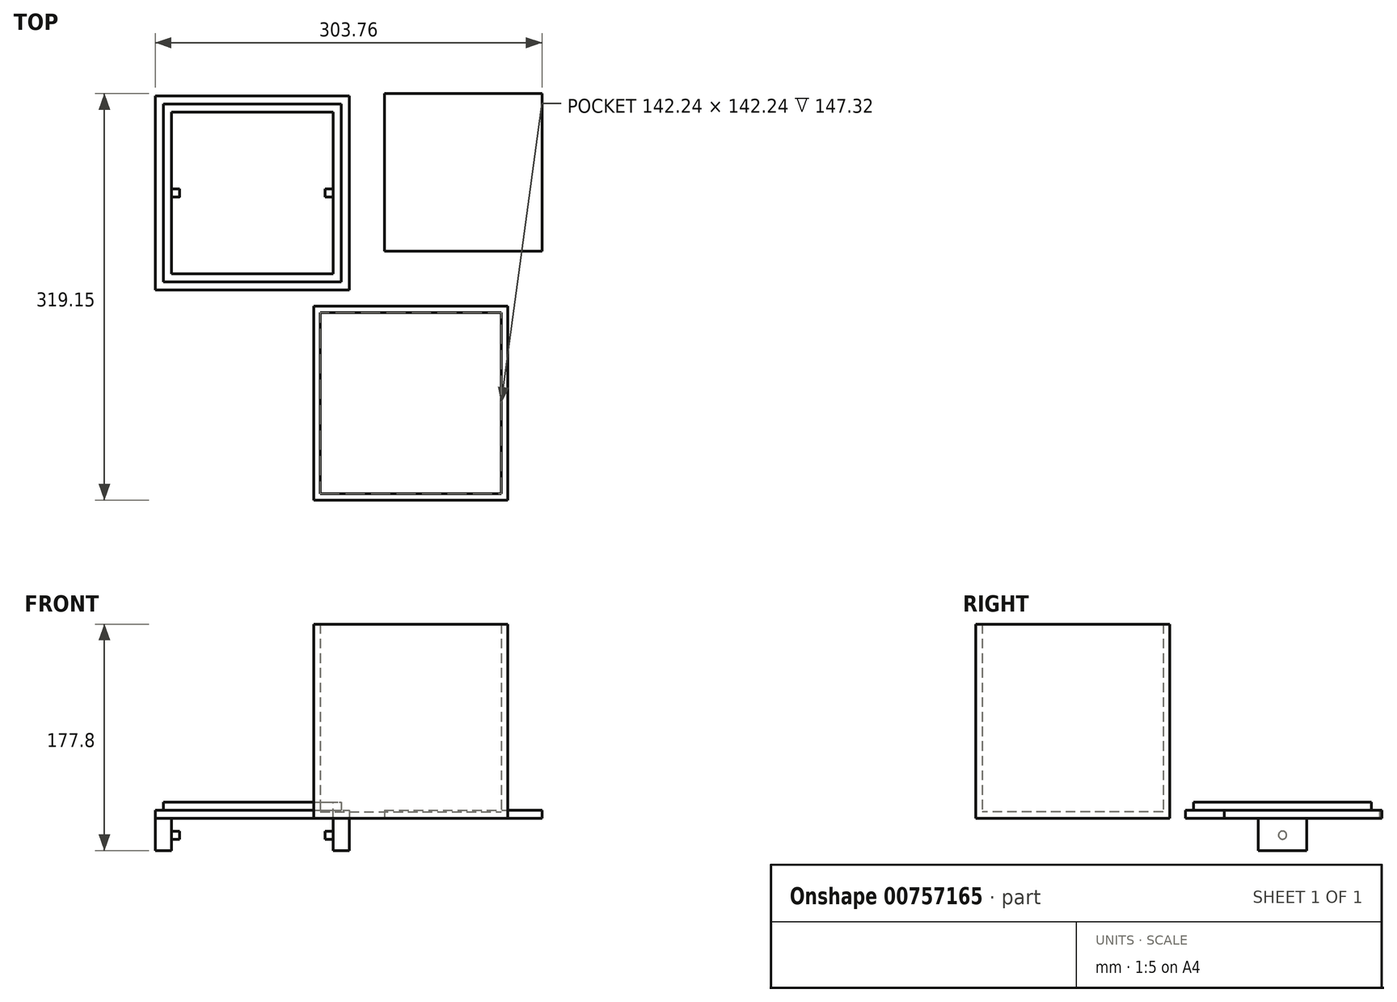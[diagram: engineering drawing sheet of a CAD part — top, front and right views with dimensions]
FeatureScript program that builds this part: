
annotation { "Feature Type Name" : "Feature", "Feature Type Description" : "" }
export const myFeature = defineFeature(function(context is Context, id is Id, definition is map)
    precondition{}
    {
        {
            var Q0;
            Q0=qCreatedBy(makeId("Top.planeOp"),FACE);
            var sketch = newSketch(context, id + "F0", { "sketchPlane" : qUnion([Q0])});
            skLineSegment(sketch, "E0.bottom", {"start": v(-92.32, 84.12) * mm, "end": v(60.08, 84.12) * mm});
            skLineSegment(sketch, "E0.top", {"start": v(-92.32, -68.28) * mm, "end": v(60.08, -68.28) * mm});
            skLineSegment(sketch, "E0.left", {"start": v(-92.32, 84.12) * mm, "end": v(-92.32, -68.28) * mm});
            skLineSegment(sketch, "E0.right", {"start": v(60.08, 84.12) * mm, "end": v(60.08, -68.28) * mm});
            skSolve(sketch);
        }
        {
            var Q0;
            Q0=makeQuery(id+"F0.imprint","IMPRINT",FACE,{"disambiguationData":[TD([[makeQuery(id+"F0.imprint","IMPRINT",EDGE,{"derivedFrom":sQuery(id+"F0.wireOp",EDGE,"E0.bottom")}),-1.0]])]});
            extrude(context, id + "F1", {"entities" : qUnion([Q0]), "depth" : 152.4 * mm, "offsetDistance" : 25.4 * mm});
        }
        {
            var Q0;
            Q0=makeQuery(id+"F1.opExtrude","CAP_FACE",FACE,{"disambiguationData":[OSD([sQuery(id+"F0.wireOp",EDGE,"E0.bottom"),sQuery(id+"F0.wireOp",EDGE,"E0.top"),sQuery(id+"F0.wireOp",EDGE,"E0.left"),sQuery(id+"F0.wireOp",EDGE,"E0.right")])],"isStart":false});
            shell(context, id + "F2", {"entities" : qUnion([Q0]), "thickness" : 5.08 * mm});
        }
        {
            var Q0;
            Q0=qCreatedBy(makeId("Top.planeOp"),FACE);
            var sketch = newSketch(context, id + "F3", { "sketchPlane" : qUnion([Q0])});
            skLineSegment(sketch, "E1.bottom", {"start": v(-216.7, 96.72) * mm, "end": v(-64.3, 96.72) * mm});
            skLineSegment(sketch, "E1.top", {"start": v(-216.7, 249.12) * mm, "end": v(-64.3, 249.12) * mm});
            skLineSegment(sketch, "E1.left", {"start": v(-216.7, 96.72) * mm, "end": v(-216.7, 249.12) * mm});
            skLineSegment(sketch, "E1.right", {"start": v(-64.3, 96.72) * mm, "end": v(-64.3, 249.12) * mm});
            skSolve(sketch);
        }
        {
            var Q0;
            Q0=makeQuery(id+"F3.imprint","IMPRINT",FACE,{"disambiguationData":[TD([[makeQuery(id+"F3.imprint","IMPRINT",EDGE,{"derivedFrom":sQuery(id+"F3.wireOp",EDGE,"E1.bottom")}),1.0]])]});
            extrude(context, id + "F4", {"entities" : qUnion([Q0]), "depth" : 6.35 * mm, "offsetDistance" : 25.4 * mm});
        }
        {
            var Q0;
            Q0=makeQuery(id+"F4.opExtrude","CAP_FACE",FACE,{"disambiguationData":[OSD([sQuery(id+"F3.wireOp",EDGE,"E1.bottom"),sQuery(id+"F3.wireOp",EDGE,"E1.top"),sQuery(id+"F3.wireOp",EDGE,"E1.left"),sQuery(id+"F3.wireOp",EDGE,"E1.right")])],"isStart":false});
            var sketch = newSketch(context, id + "F5", { "sketchPlane" : qUnion([Q0])});
            skLineSegment(sketch, "E2.bottom", {"start": v(-210.36, 242.77) * mm, "end": v(-70.66, 242.77) * mm});
            skLineSegment(sketch, "E2.top", {"start": v(-210.36, 103.07) * mm, "end": v(-70.66, 103.07) * mm});
            skLineSegment(sketch, "E2.left", {"start": v(-210.36, 242.77) * mm, "end": v(-210.36, 103.07) * mm});
            skLineSegment(sketch, "E2.right", {"start": v(-70.66, 242.77) * mm, "end": v(-70.66, 103.07) * mm});
            skSolve(sketch);
        }
        {
            var Q0;
            Q0=makeQuery(id+"F5.imprint","IMPRINT",FACE,{"disambiguationData":[TD([[makeQuery(id+"F5.imprint","IMPRINT",EDGE,{"derivedFrom":sQuery(id+"F5.wireOp",EDGE,"E2.bottom")}),-1.0]])]});
            extrude(context, id + "F6", {"entities" : qUnion([Q0]), "operationType" : NewBodyOperationType.ADD, "depth" : 6.35 * mm, "offsetDistance" : 25.4 * mm});
        }
        {
            var Q0;
            Q0=makeQuery(id+"F6.opExtrude","CAP_FACE",FACE,{"disambiguationData":[OSD([sQuery(id+"F5.wireOp",EDGE,"E2.bottom"),sQuery(id+"F5.wireOp",EDGE,"E2.top"),sQuery(id+"F5.wireOp",EDGE,"E2.left"),sQuery(id+"F5.wireOp",EDGE,"E2.right")])],"isStart":false});
            var sketch = newSketch(context, id + "F7", { "sketchPlane" : qUnion([Q0])});
            skLineSegment(sketch, "E3.bottom", {"start": v(-204, 236.42) * mm, "end": v(-77, 236.42) * mm});
            skLineSegment(sketch, "E3.top", {"start": v(-204, 109.42) * mm, "end": v(-77, 109.42) * mm});
            skLineSegment(sketch, "E3.left", {"start": v(-204, 236.42) * mm, "end": v(-204, 109.42) * mm});
            skLineSegment(sketch, "E3.right", {"start": v(-77, 236.42) * mm, "end": v(-77, 109.42) * mm});
            skSolve(sketch);
        }
        {
            var Q0;
            Q0=makeQuery(id+"F7.imprint","IMPRINT",FACE,{"disambiguationData":[TD([[makeQuery(id+"F7.imprint","IMPRINT",EDGE,{"derivedFrom":sQuery(id+"F7.wireOp",EDGE,"E3.bottom")}),-1.0]])]});
            extrude(context, id + "F8", {"entities" : qUnion([Q0]), "operationType" : NewBodyOperationType.REMOVE, "oppositeDirection" : true, "depth" : 25.4 * mm, "offsetDistance" : 25.4 * mm});
        }
        {
            var Q0;
            Q0=makeQuery(id+"F4.opExtrude","CAP_FACE",FACE,{"disambiguationData":[OSD([sQuery(id+"F3.wireOp",EDGE,"E1.bottom"),sQuery(id+"F3.wireOp",EDGE,"E1.top"),sQuery(id+"F3.wireOp",EDGE,"E1.left"),sQuery(id+"F3.wireOp",EDGE,"E1.right")])],"isStart":true});
            var sketch = newSketch(context, id + "F9", { "sketchPlane" : qUnion([Q0])});
            skLineSegment(sketch, "E4.bottom", {"start": v(-216.7, -153.87) * mm, "end": v(-204, -153.87) * mm});
            skLineSegment(sketch, "E4.top", {"start": v(-216.7, -191.97) * mm, "end": v(-204, -191.97) * mm});
            skLineSegment(sketch, "E4.left", {"start": v(-216.7, -153.87) * mm, "end": v(-216.7, -191.97) * mm});
            skLineSegment(sketch, "E4.right", {"start": v(-204, -153.87) * mm, "end": v(-204, -191.97) * mm});
            skLineSegment(sketch, "E5.bottom", {"start": v(-77, -153.87) * mm, "end": v(-64.3, -153.87) * mm});
            skLineSegment(sketch, "E5.top", {"start": v(-77, -191.97) * mm, "end": v(-64.3, -191.97) * mm});
            skLineSegment(sketch, "E5.left", {"start": v(-77, -153.87) * mm, "end": v(-77, -191.97) * mm});
            skLineSegment(sketch, "E5.right", {"start": v(-64.3, -153.87) * mm, "end": v(-64.3, -191.97) * mm});
            skSolve(sketch);
        }
        {
            var Q0;
            Q0=makeQuery(id+"F9.imprint","IMPRINT",FACE,{"disambiguationData":[TD([[makeQuery(id+"F9.imprint","IMPRINT",EDGE,{"derivedFrom":sQuery(id+"F9.wireOp",EDGE,"E4.bottom")}),-1.0]])]});
            var Q1;
            Q1=makeQuery(id+"F9.imprint","IMPRINT",FACE,{"disambiguationData":[TD([[makeQuery(id+"F9.imprint","IMPRINT",EDGE,{"derivedFrom":sQuery(id+"F9.wireOp",EDGE,"E5.bottom")}),-1.0]])]});
            extrude(context, id + "F10", {"entities" : qUnion([Q0, Q1]), "operationType" : NewBodyOperationType.ADD, "depth" : 25.4 * mm, "offsetDistance" : 25.4 * mm});
        }
        {
            var Q0;
            Q0=makeQuery(id+"F10.boolean.opBoolean","MERGE",FACE,{"derivedFrom":[makeQuery(id+"F8.boolean.opBoolean","COPY",FACE,{"derivedFrom":makeQuery(id+"F8.opExtrude","SWEPT_FACE",FACE,{"disambiguationData":[OSD([sQuery(id+"F7.wireOp",EDGE,"E3.right")])]})}),makeQuery(id+"F10.opExtrude","SWEPT_FACE",FACE,{"disambiguationData":[OSD([sQuery(id+"F9.wireOp",EDGE,"E5.left")])]})]});
            var sketch = newSketch(context, id + "F11", { "sketchPlane" : qUnion([Q0])});
            skCircle(sketch, "E6", {"center": v(-172.92, -13.34) * mm, "radius": 3.18 * mm});
            skSolve(sketch);
        }
        {
            var Q0;
            Q0=makeQuery(id+"F10.boolean.opBoolean","MERGE",FACE,{"derivedFrom":[makeQuery(id+"F8.boolean.opBoolean","COPY",FACE,{"derivedFrom":makeQuery(id+"F8.opExtrude","SWEPT_FACE",FACE,{"disambiguationData":[OSD([sQuery(id+"F7.wireOp",EDGE,"E3.left")])]})}),makeQuery(id+"F10.opExtrude","SWEPT_FACE",FACE,{"disambiguationData":[OSD([sQuery(id+"F9.wireOp",EDGE,"E4.right")])]})]});
            var sketch = newSketch(context, id + "F12", { "sketchPlane" : qUnion([Q0])});
            skCircle(sketch, "E7", {"center": v(172.92, -13.34) * mm, "radius": 3.18 * mm});
            skSolve(sketch);
        }
        {
            var Q0;
            Q0=makeQuery(id+"F11.imprint","IMPRINT",FACE,{"disambiguationData":[TD([[makeQuery(id+"F11.imprint","IMPRINT",EDGE,{"derivedFrom":sQuery(id+"F11.wireOp",EDGE,"E6")}),1.0]])]});
            extrude(context, id + "F13", {"entities" : qUnion([Q0]), "operationType" : NewBodyOperationType.ADD, "depth" : 6.35 * mm, "offsetDistance" : 25.4 * mm});
        }
        {
            var Q0;
            Q0=makeQuery(id+"F12.imprint","IMPRINT",FACE,{"disambiguationData":[TD([[makeQuery(id+"F12.imprint","IMPRINT",EDGE,{"derivedFrom":sQuery(id+"F12.wireOp",EDGE,"E7")}),1.0]])]});
            extrude(context, id + "F14", {"entities" : qUnion([Q0]), "operationType" : NewBodyOperationType.ADD, "depth" : 6.35 * mm, "offsetDistance" : 25.4 * mm});
        }
        {
            var Q0;
            Q0=qCreatedBy(makeId("Top.planeOp"),FACE);
            var sketch = newSketch(context, id + "F15", { "sketchPlane" : qUnion([Q0])});
            skLineSegment(sketch, "E8.bottom", {"start": v(-36.77, 250.87) * mm, "end": v(87.05, 250.87) * mm});
            skLineSegment(sketch, "E8.top", {"start": v(-36.77, 127.04) * mm, "end": v(87.05, 127.04) * mm});
            skLineSegment(sketch, "E8.left", {"start": v(-36.77, 250.87) * mm, "end": v(-36.77, 127.04) * mm});
            skLineSegment(sketch, "E8.right", {"start": v(87.05, 250.87) * mm, "end": v(87.05, 127.04) * mm});
            skSolve(sketch);
        }
        {
            var Q0;
            Q0=makeQuery(id+"F15.imprint","IMPRINT",FACE,{"disambiguationData":[TD([[makeQuery(id+"F15.imprint","IMPRINT",EDGE,{"derivedFrom":sQuery(id+"F15.wireOp",EDGE,"E8.bottom")}),-1.0]])]});
            extrude(context, id + "F16", {"entities" : qUnion([Q0]), "depth" : 6.35 * mm, "offsetDistance" : 25.4 * mm});
        }
    });
